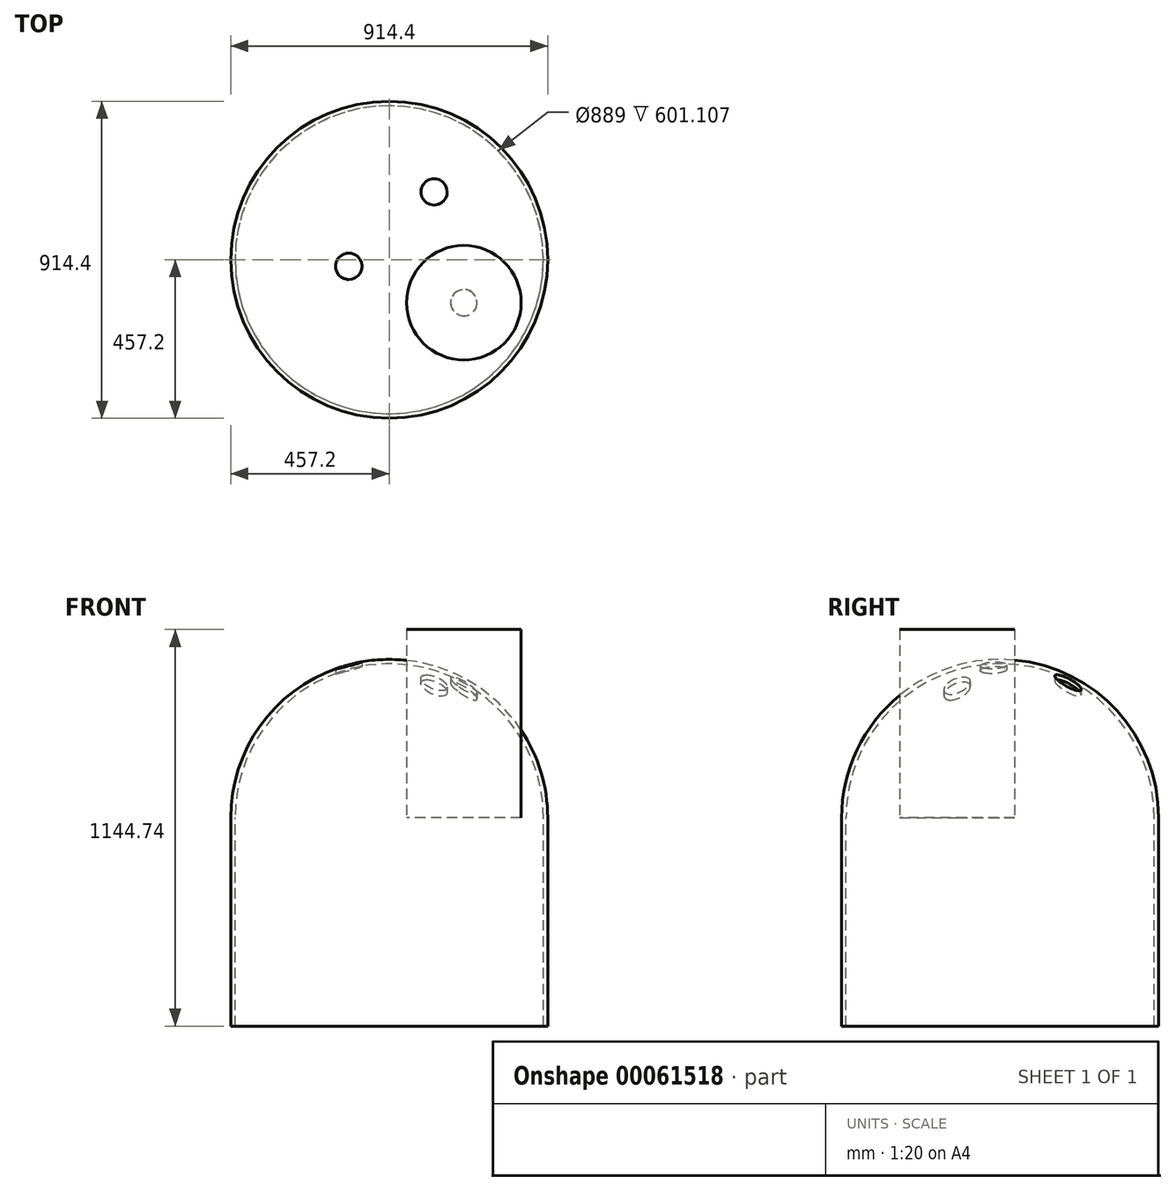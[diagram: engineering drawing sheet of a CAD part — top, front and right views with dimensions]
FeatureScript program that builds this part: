
annotation { "Feature Type Name" : "Feature", "Feature Type Description" : "" }
export const myFeature = defineFeature(function(context is Context, id is Id, definition is map)
    precondition{}
    {
        {
            var Q0;
            Q0=qCreatedBy(makeId("Top.planeOp"),FACE);
            var sketch = newSketch(context, id + "F0", { "sketchPlane" : qUnion([Q0])});
            skLineSegment(sketch, "E0", {"start": v(0, -609.6) * mm, "end": v(0, 609.6) * mm, "construction": true});
            skArc(sketch, "E1", {"start": v(0, -457.2) * mm, "mid": v(457.2, 0) * mm, "end": v(0, 457.2) * mm});
            skArc(sketch, "E2.0", {"start": v(0, -444.5) * mm, "mid": v(444.5, 0) * mm, "end": v(0, 444.5) * mm});
            skLineSegment(sketch, "E3", {"start": v(0, -457.2) * mm, "end": v(0, -444.5) * mm});
            skLineSegment(sketch, "E4", {"start": v(0, 444.5) * mm, "end": v(0, 457.2) * mm});
            skPoint(sketch, "E5", {"position": v(0, 163.9) * mm});
            skSolve(sketch);
        }
        {
            var Q0;
            Q0 = qSketchRegion(id + "F0", true);
            var Q1;
            Q1=sQuery(id+"F0.wireOp",EDGE,"E0");
            revolve(context, id + "F1", {"entities" : qUnion([Q0]), "axis" : qUnion([Q1]), "revolveType" : RevolveType.ONE_DIRECTION, "oppositeDirection" : true, "angle" : 180 * degree});
        }
        {
            var Q0;
            Q0=qCreatedBy(makeId("Top.planeOp"),FACE);
            var sketch = newSketch(context, id + "F2", { "sketchPlane" : qUnion([Q0])});
            skPoint(sketch, "E6", {"position": v(-116.6, -18.99) * mm});
            skPoint(sketch, "E7", {"position": v(215.27, -124) * mm});
            skPoint(sketch, "E8", {"position": v(129.35, 195.92) * mm});
            skSolve(sketch);
        }
        {
            var Q0;
            Q0=sQuery(id+"F2.wireOp",VERTEX,"E6");
            var Q1;
            Q1=sQuery(id+"F2.wireOp",VERTEX,"E8");
            var Q2;
            Q2=sQuery(id+"F2.wireOp",VERTEX,"E7");
            var Q3;
            Q3=makeQuery(id+"F1.opRevolve","SWEPT_BODY",BODY,{"disambiguationData":[OSD([sQuery(id+"F0.wireOp",EDGE,"E1"),sQuery(id+"F0.wireOp",EDGE,"E2.0"),sQuery(id+"F0.wireOp",EDGE,"E3"),sQuery(id+"F0.wireOp",EDGE,"E4")])]});
            hole(context, id + "F3", {"style" : HoleStyle.SIMPLE, "holeDiameter" : 76.2 * mm, "endStyle" : HoleEndStyle.THROUGH, "oppositeDirection" : true, "locations" : qUnion([Q0, Q1, Q2]), "scope" : qUnion([Q3])});
        }
        {
            var Q0;
            Q0=qCreatedBy(makeId("Top.planeOp"),FACE);
            var sketch = newSketch(context, id + "F4", { "sketchPlane" : qUnion([Q0])});
            skCircle(sketch, "E9", {"center": v(215.27, -124) * mm, "radius": 165.23 * mm});
            skSolve(sketch);
        }
        {
            var Q0;
            Q0=makeQuery(id+"F4.imprint","IMPRINT",FACE,{"disambiguationData":[TD([[makeQuery(id+"F4.imprint","IMPRINT",EDGE,{"derivedFrom":sQuery(id+"F4.wireOp",EDGE,"E9")}),1.0]])]});
            extrude(context, id + "F5", {"entities" : qUnion([Q0]), "depth" : 543.63 * mm});
        }
        {
            var Q0;
            Q0=makeQuery(id+"F1.opRevolve","CAP_FACE",FACE,{"disambiguationData":[OSD([sQuery(id+"F0.wireOp",EDGE,"E1"),sQuery(id+"F0.wireOp",EDGE,"E2.0"),sQuery(id+"F0.wireOp",EDGE,"E3"),sQuery(id+"F0.wireOp",EDGE,"E4")])],"isStart":true});
            extrude(context, id + "F6", {"entities" : qUnion([Q0]), "operationType" : NewBodyOperationType.ADD, "depth" : 601.1 * mm});
        }
    });
